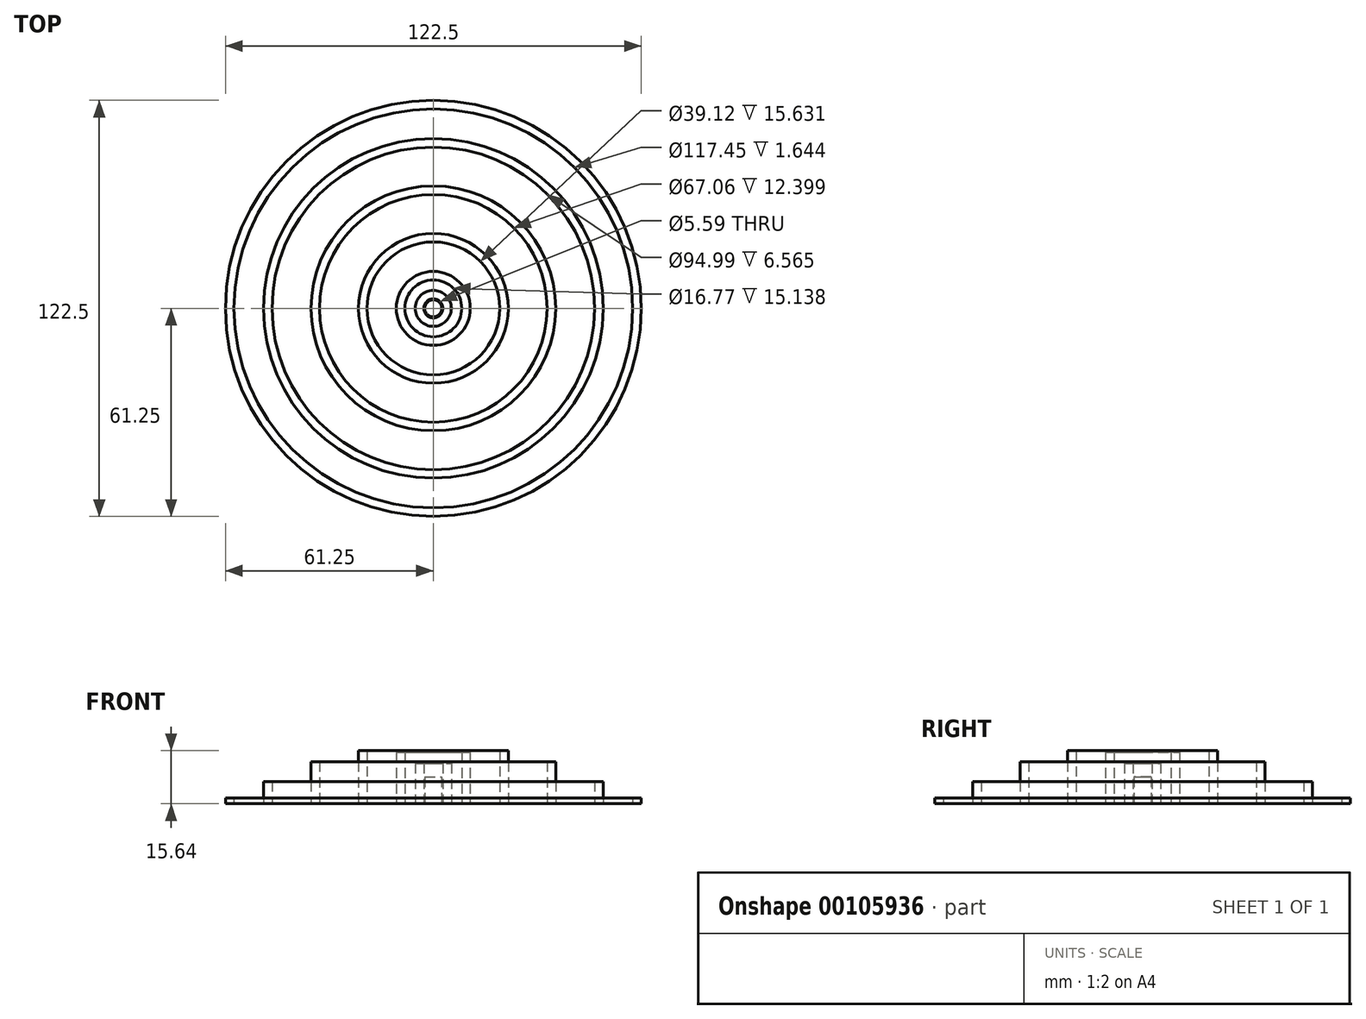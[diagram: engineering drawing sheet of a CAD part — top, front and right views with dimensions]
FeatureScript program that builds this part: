
annotation { "Feature Type Name" : "Feature", "Feature Type Description" : "" }
export const myFeature = defineFeature(function(context is Context, id is Id, definition is map)
    precondition{}
    {
        {
            var Q0;
            Q0=qCreatedBy(makeId("Front.planeOp"),FACE);
            var sketch = newSketch(context, id + "F0", { "sketchPlane" : qUnion([Q0])});
            skLineSegment(sketch, "E0", {"start": v(0, 7.88) * mm, "end": v(0.01, 7.88) * mm});
            skLineSegment(sketch, "E1", {"start": v(2.5, 7.88) * mm, "end": v(2.5, 0) * mm});
            skLineSegment(sketch, "E2", {"start": v(2.8, 11.91) * mm, "end": v(5.3, 11.91) * mm});
            skLineSegment(sketch, "E3", {"start": v(5.3, 11.91) * mm, "end": v(5.3, 0) * mm});
            skLineSegment(sketch, "E4", {"start": v(5.3, 0) * mm, "end": v(2.8, 0) * mm});
            skLineSegment(sketch, "E5", {"start": v(2.8, 0) * mm, "end": v(2.8, 11.91) * mm});
            skLineSegment(sketch, "E6", {"start": v(8.38, 15.15) * mm, "end": v(10.89, 15.15) * mm});
            skLineSegment(sketch, "E7", {"start": v(10.89, 15.15) * mm, "end": v(10.89, 0) * mm});
            skLineSegment(sketch, "E8", {"start": v(10.89, 0) * mm, "end": v(8.38, 0) * mm});
            skLineSegment(sketch, "E9", {"start": v(8.38, 0) * mm, "end": v(8.38, 15.15) * mm});
            skLineSegment(sketch, "E10", {"start": v(19.56, 15.64) * mm, "end": v(22.06, 15.64) * mm});
            skLineSegment(sketch, "E11", {"start": v(22.06, 15.64) * mm, "end": v(22.06, 0) * mm});
            skLineSegment(sketch, "E12", {"start": v(22.06, 0) * mm, "end": v(19.56, 0) * mm});
            skLineSegment(sketch, "E13", {"start": v(19.56, 0) * mm, "end": v(19.56, 15.64) * mm});
            skLineSegment(sketch, "E14", {"start": v(33.53, 12.4) * mm, "end": v(36.03, 12.4) * mm});
            skLineSegment(sketch, "E15", {"start": v(36.03, 12.4) * mm, "end": v(36.03, 0) * mm});
            skLineSegment(sketch, "E16", {"start": v(36.03, 0) * mm, "end": v(33.53, 0) * mm});
            skLineSegment(sketch, "E17", {"start": v(33.53, 0) * mm, "end": v(33.53, 12.4) * mm});
            skLineSegment(sketch, "E18", {"start": v(47.5, 6.57) * mm, "end": v(50, 6.57) * mm});
            skLineSegment(sketch, "E19", {"start": v(50, 6.57) * mm, "end": v(50, 0) * mm});
            skLineSegment(sketch, "E20", {"start": v(50, 0) * mm, "end": v(47.5, 0) * mm});
            skLineSegment(sketch, "E21", {"start": v(47.5, 0) * mm, "end": v(47.5, 6.57) * mm});
            skLineSegment(sketch, "E22", {"start": v(58.73, 1.7) * mm, "end": v(61.25, 1.7) * mm});
            skLineSegment(sketch, "E23", {"start": v(61.25, 1.7) * mm, "end": v(61.25, 0.06) * mm});
            skLineSegment(sketch, "E24", {"start": v(61.25, 0.06) * mm, "end": v(58.73, 0.06) * mm});
            skLineSegment(sketch, "E25", {"start": v(58.73, 0.06) * mm, "end": v(58.73, 1.7) * mm});
            skLineSegment(sketch, "E26.bottom", {"start": v(0, 0) * mm, "end": v(2.5, 0) * mm});
            skLineSegment(sketch, "E26.top", {"start": v(0, 7.88) * mm, "end": v(2.5, 7.88) * mm});
            skLineSegment(sketch, "E26.left", {"start": v(0, 0) * mm, "end": v(0, 7.88) * mm});
            skLineSegment(sketch, "E26.right", {"start": v(2.5, 0) * mm, "end": v(2.5, 7.88) * mm});
            skLineSegment(sketch, "E27", {"start": v(0, 0) * mm, "end": v(0, 21.77) * mm, "construction": true});
            skSolve(sketch);
        }
        {
            var Q0;
            {var subQ0=sQuery(id+"F0.wireOp",EDGE,"E26.bottom");Q0=makeQuery(id+"F0.imprint","IMPRINT",FACE,{"disambiguationData":[TD([[makeQuery(id+"F0.imprint","IMPRINT",EDGE,{"derivedFrom":subQ0}),1.0]])]});}
            var Q1;
            Q1=makeQuery(id+"F0.imprint","IMPRINT",FACE,{"disambiguationData":[TD([[makeQuery(id+"F0.imprint","IMPRINT",EDGE,{"derivedFrom":sQuery(id+"F0.wireOp",EDGE,"E2")}),-1.0]])]});
            var Q2;
            Q2=makeQuery(id+"F0.imprint","IMPRINT",FACE,{"disambiguationData":[TD([[makeQuery(id+"F0.imprint","IMPRINT",EDGE,{"derivedFrom":sQuery(id+"F0.wireOp",EDGE,"E6")}),-1.0]])]});
            var Q3;
            Q3=makeQuery(id+"F0.imprint","IMPRINT",FACE,{"disambiguationData":[TD([[makeQuery(id+"F0.imprint","IMPRINT",EDGE,{"derivedFrom":sQuery(id+"F0.wireOp",EDGE,"E10")}),-1.0]])]});
            var Q4;
            Q4=makeQuery(id+"F0.imprint","IMPRINT",FACE,{"disambiguationData":[TD([[makeQuery(id+"F0.imprint","IMPRINT",EDGE,{"derivedFrom":sQuery(id+"F0.wireOp",EDGE,"E14")}),-1.0]])]});
            var Q5;
            Q5=makeQuery(id+"F0.imprint","IMPRINT",FACE,{"disambiguationData":[TD([[makeQuery(id+"F0.imprint","IMPRINT",EDGE,{"derivedFrom":sQuery(id+"F0.wireOp",EDGE,"E18")}),-1.0]])]});
            var Q6;
            Q6=makeQuery(id+"F0.imprint","IMPRINT",FACE,{"disambiguationData":[TD([[makeQuery(id+"F0.imprint","IMPRINT",EDGE,{"derivedFrom":sQuery(id+"F0.wireOp",EDGE,"E22")}),-1.0]])]});
            var Q7;
            Q7=sQuery(id+"F0.wireOp",EDGE,"E27");
            revolve(context, id + "F1", {"entities" : qUnion([Q0, Q1, Q2, Q3, Q4, Q5, Q6]), "axis" : qUnion([Q7]), "revolveType" : RevolveType.FULL});
        }
    });
